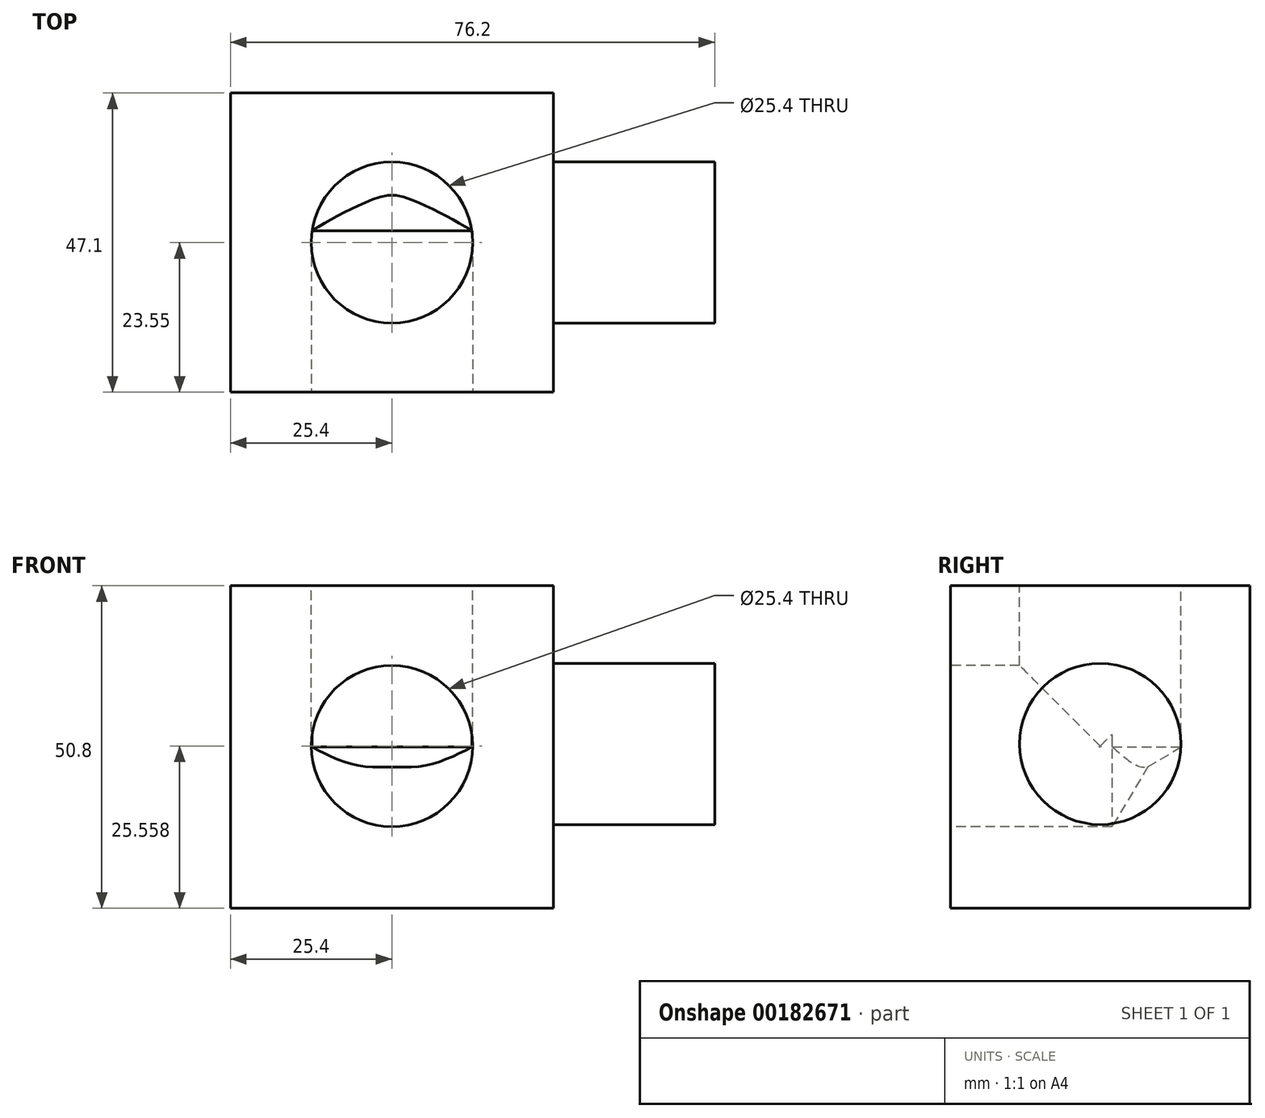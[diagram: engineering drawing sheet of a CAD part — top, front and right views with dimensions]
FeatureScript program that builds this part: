
annotation { "Feature Type Name" : "Feature", "Feature Type Description" : "" }
export const myFeature = defineFeature(function(context is Context, id is Id, definition is map)
    precondition{}
    {
        {
            var Q0;
            Q0=qCreatedBy(makeId("Top.planeOp"),FACE);
            var sketch = newSketch(context, id + "F0", { "sketchPlane" : qUnion([Q0])});
            skLineSegment(sketch, "E0.bottom", {"start": v(25.4, 23.55) * mm, "end": v(-25.4, 23.55) * mm});
            skLineSegment(sketch, "E0.top", {"start": v(25.4, -23.55) * mm, "end": v(-25.4, -23.55) * mm});
            skLineSegment(sketch, "E0.left", {"start": v(25.4, 23.55) * mm, "end": v(25.4, -23.55) * mm});
            skLineSegment(sketch, "E0.right", {"start": v(-25.4, 23.55) * mm, "end": v(-25.4, -23.55) * mm});
            skPoint(sketch, "E0.middle", {"position": v(0, 0) * mm});
            skSolve(sketch);
        }
        {
            var Q0;
            Q0 = qSketchRegion(id + "F0", true);
            extrude(context, id + "F1", {"entities" : qUnion([Q0]), "depth" : 50.8 * mm});
        }
        {
            var Q0;
            Q0=makeQuery(id+"F1.opExtrude","CAP_FACE",FACE,{"disambiguationData":[OSD([sQuery(id+"F0.wireOp",EDGE,"E0.bottom"),sQuery(id+"F0.wireOp",EDGE,"E0.top"),sQuery(id+"F0.wireOp",EDGE,"E0.left"),sQuery(id+"F0.wireOp",EDGE,"E0.right")])],"isStart":false});
            var sketch = newSketch(context, id + "F2", { "sketchPlane" : qUnion([Q0])});
            skCircle(sketch, "E1", {"center": v(0, 0) * mm, "radius": 12.7 * mm});
            skSolve(sketch);
        }
        {
            var Q0;
            Q0=sQuery(id+"F2.wireOp",VERTEX,"E1.center");
            var Q1;
            Q1=makeQuery(id+"F1.opExtrude","SWEPT_BODY",BODY,{"disambiguationData":[OSD([sQuery(id+"F0.wireOp",EDGE,"E0.bottom"),sQuery(id+"F0.wireOp",EDGE,"E0.top"),sQuery(id+"F0.wireOp",EDGE,"E0.left"),sQuery(id+"F0.wireOp",EDGE,"E0.right")])]});
            hole(context, id + "F3", {"style" : HoleStyle.SIMPLE, "endStyle" : HoleEndStyle.BLIND, "holeDiameter" : 25.4 * mm, "holeDepth" : 25.4 * mm, "locations" : qUnion([Q0]), "scope" : qUnion([Q1])});
        }
        {
            var Q0;
            Q0=makeQuery(id+"F1.opExtrude","SWEPT_FACE",FACE,{"disambiguationData":[OSD([sQuery(id+"F0.wireOp",EDGE,"E0.top")])]});
            var sketch = newSketch(context, id + "F4", { "sketchPlane" : qUnion([Q0])});
            skLineSegment(sketch, "E2", {"start": v(0, 0) * mm, "end": v(0, 25.4) * mm});
            skPoint(sketch, "E2.endSnap0", {"position": v(0, 0) * mm});
            skSolve(sketch);
        }
        {
            var Q0;
            {var subQ0=sQuery(id+"F0.wireOp",EDGE,"E0.top");Q0=makeQuery(id+"F4.imprint","IMPRINT",FACE,{"disambiguationData":[TD([[makeQuery(id+"F4.imprint","IMPRINT",EDGE,{"derivedFrom":makeQuery(id+"F1.opExtrude","CAP_EDGE",EDGE,{"disambiguationData":[OSD([subQ0])],"isStart":false})}),1.0]])]});}
            var sketch = newSketch(context, id + "F5", { "sketchPlane" : qUnion([Q0])});
            skCircle(sketch, "E3", {"center": v(0, 25.56) * mm, "radius": 12.7 * mm});
            skSolve(sketch);
        }
        {
            var Q0;
            Q0=sQuery(id+"F5.wireOp",VERTEX,"E3.center");
            var Q1;
            Q1=makeQuery(id+"F1.opExtrude","SWEPT_BODY",BODY,{"disambiguationData":[OSD([sQuery(id+"F0.wireOp",EDGE,"E0.bottom"),sQuery(id+"F0.wireOp",EDGE,"E0.top"),sQuery(id+"F0.wireOp",EDGE,"E0.left"),sQuery(id+"F0.wireOp",EDGE,"E0.right")])]});
            hole(context, id + "F6", {"style" : HoleStyle.SIMPLE, "endStyle" : HoleEndStyle.BLIND, "holeDiameter" : 25.4 * mm, "holeDepth" : 25.4 * mm, "locations" : qUnion([Q0]), "scope" : qUnion([Q1])});
        }
        {
            var Q0;
            Q0=makeQuery(id+"F1.opExtrude","SWEPT_FACE",FACE,{"disambiguationData":[OSD([sQuery(id+"F0.wireOp",EDGE,"E0.left")])]});
            var sketch = newSketch(context, id + "F7", { "sketchPlane" : qUnion([Q0])});
            skLineSegment(sketch, "E4", {"start": v(0, 0) * mm, "end": v(0, 25.4) * mm});
            skSolve(sketch);
        }
        {
            var Q0;
            {var subQ0=sQuery(id+"F0.wireOp",EDGE,"E0.left");Q0=makeQuery(id+"F7.imprint","IMPRINT",FACE,{"disambiguationData":[TD([[makeQuery(id+"F7.imprint","IMPRINT",EDGE,{"derivedFrom":makeQuery(id+"F1.opExtrude","CAP_EDGE",EDGE,{"disambiguationData":[OSD([subQ0])],"isStart":false})}),1.0]])]});}
            var sketch = newSketch(context, id + "F8", { "sketchPlane" : qUnion([Q0])});
            skCircle(sketch, "E5", {"center": v(0, 25.9) * mm, "radius": 12.7 * mm});
            skSolve(sketch);
        }
        {
            var Q0;
            Q0 = qSketchRegion(id + "F8", true);
            extrude(context, id + "F9", {"entities" : qUnion([Q0]), "operationType" : NewBodyOperationType.ADD, "depth" : 25.4 * mm});
        }
    });
